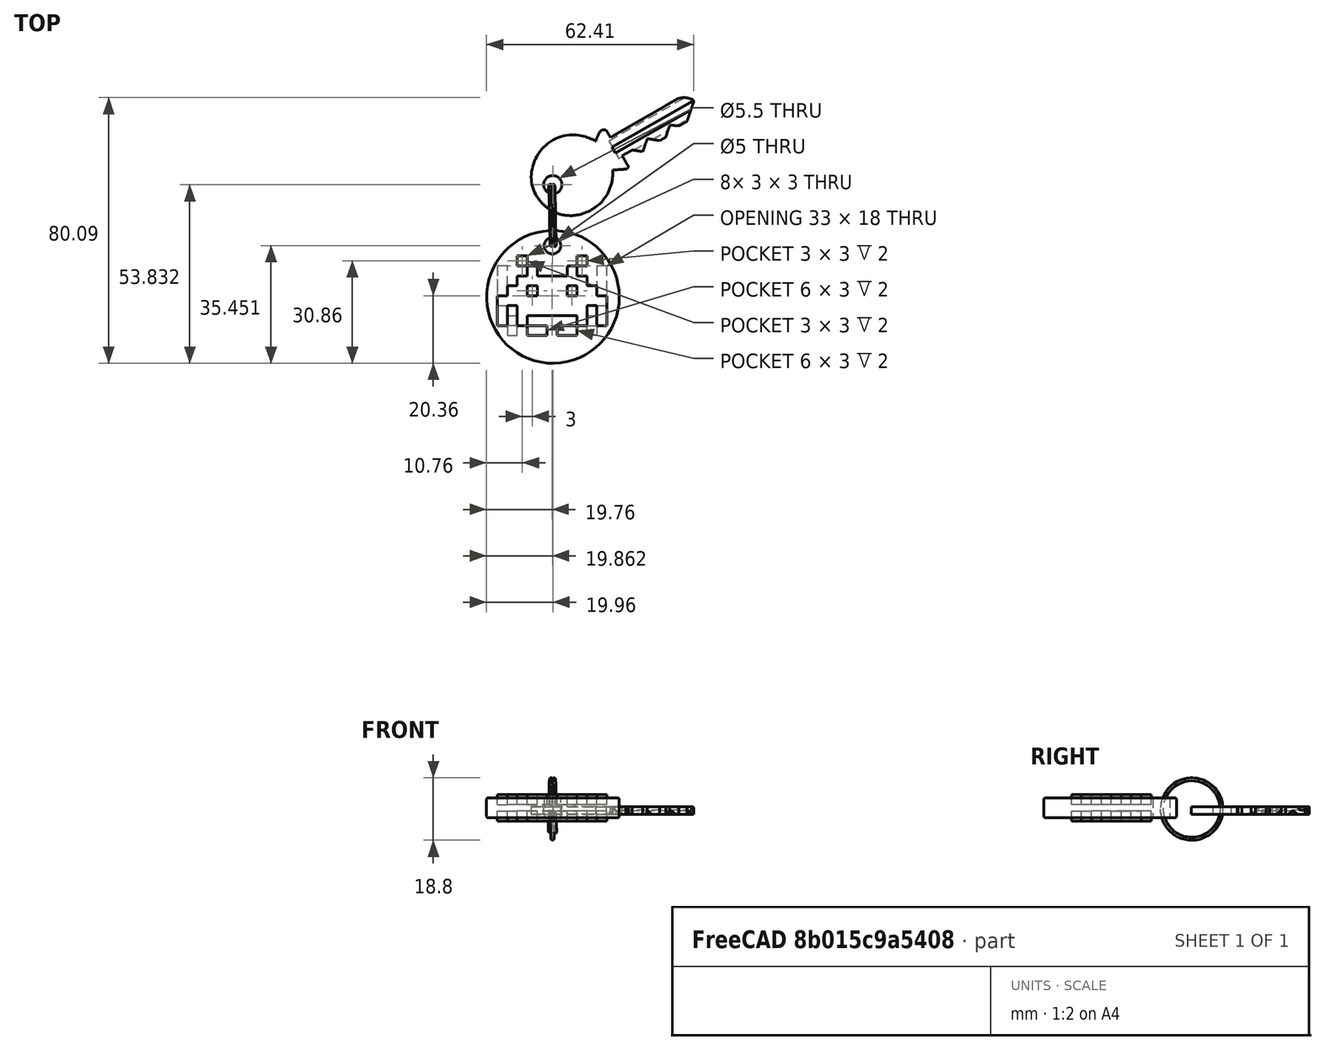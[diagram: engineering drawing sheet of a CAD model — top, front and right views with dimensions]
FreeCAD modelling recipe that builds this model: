
FCSTD DOCUMENT  (FreeCAD 0.15R4671 (Git))
Label: space_invaders
License: All rights reserved
LicenseURL: http://en.wikipedia.org/wiki/All_rights_reserved
objects: Part::Fuse×2, Part::Feature×2, Part::Cut×1, Part::MultiFuse×1, PartDesign::Fillet×1
note: 7 computed .brp shape members not serialized (recipe doc carries the construction recipe); baked Part::Feature solids carry a one-line shape summary decoded from their .brp

FEATURE [Part::Fuse] Fusion  label="Invader front"
  Placement = pos=(-0.5,-0.5,1) rot=(0,0,1;0rad)
FEATURE [Part::Fuse] Fusion002  label="Invader back"
  Placement = pos=(-48.5,-0.5,-4) rot=(0,0,1;0rad)
FEATURE [Part::Cut] Cut  label="Fondo"
FEATURE [Part::Feature] Cut001  label="key-model"
  Placement = pos=(-5.46976,31.0266,0) rot=(0,0,1;0.517888rad)
  shape: bbox 49.82 x 36.6 x 2.3 mm, 44 faces (baked)
FEATURE [Part::Feature] Sweep  label="key-ring-model"
  Placement = pos=(-1.2,24.7546,1.6391) rot=(0.333333,0.881918,0.333333;1.69612rad)
  shape: bbox 3.31 x 27.02 x 26.33 mm, 4 faces (baked)
FEATURE [Part::MultiFuse] Fusion003  label="Llave"
  Placement = pos=(-28.5,20,-2) rot=(0,0,1;0rad)
  Shapes = -> [Cut001,Sweep]
FEATURE [PartDesign::Fillet] Fillet
  Base = -> Cut [Edge2,Edge3]
  Radius = 0.5
